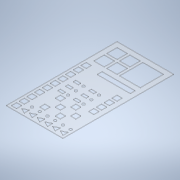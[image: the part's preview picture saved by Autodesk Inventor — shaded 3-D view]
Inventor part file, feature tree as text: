
AUTODESK INVENTOR PART (.ipt)
format: ipt  version: 2021 (Build 250183000, 183)  size: 278,016 bytes
history: native  units: mm
features: extrude x1, sketch x1
ambient origin geometry x8: Origin, YZ Plane, XZ Plane, XY Plane, X Axis, Y Axis, Z Axis, Center Point
bodies: Solid1 (feature_tree)
feature tree (2):
  extrude  "Extrusion1"  Depth=430.0mm
  sketch  "Sketch1"  dims[d0=220.0mm d1=430.0mm d28=128.0mm d29=2.5mm d30=0.0mm d31=0.5mm d32=0.872665mm]
